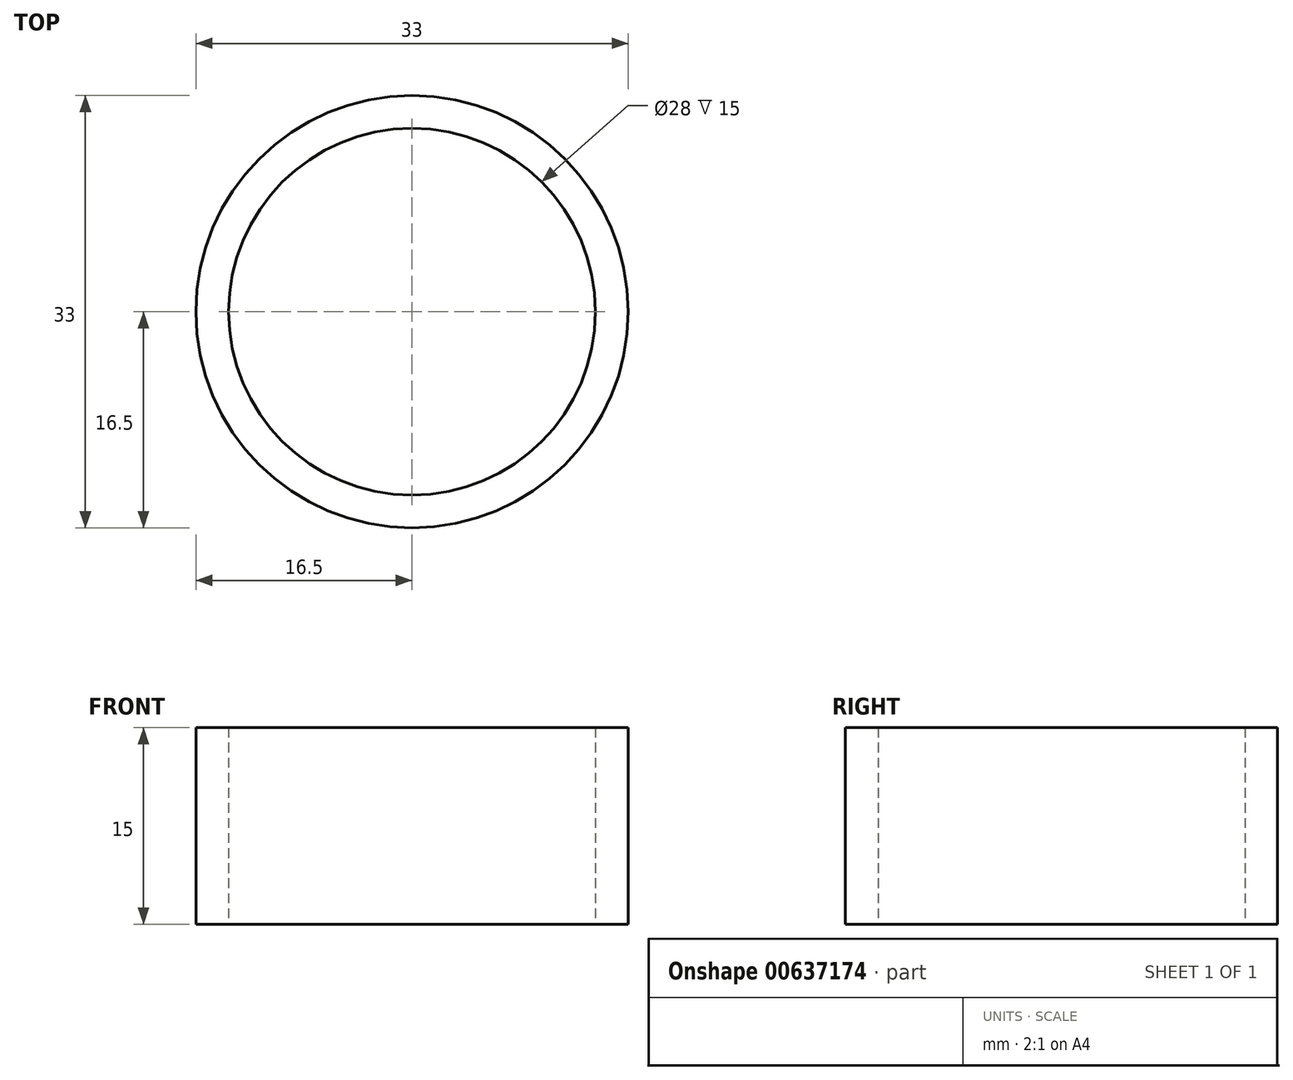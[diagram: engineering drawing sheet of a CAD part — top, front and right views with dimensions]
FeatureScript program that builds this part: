
annotation { "Feature Type Name" : "Feature", "Feature Type Description" : "" }
export const myFeature = defineFeature(function(context is Context, id is Id, definition is map)
    precondition{}
    {
        {
            var Q0;
            Q0=qCreatedBy(makeId("Top.planeOp"),FACE);
            var sketch = newSketch(context, id + "F0", { "sketchPlane" : qUnion([Q0])});
            skCircle(sketch, "E0", {"center": v(0, 0) * mm, "radius": 16.5 * mm});
            skCircle(sketch, "E1", {"center": v(0, 0) * mm, "radius": 14 * mm});
            skSolve(sketch);
        }
        {
            var Q0;
            Q0=makeQuery(id+"F0.imprint","IMPRINT",FACE,{"disambiguationData":[TD([[makeQuery(id+"F0.imprint","IMPRINT",EDGE,{"derivedFrom":sQuery(id+"F0.wireOp",EDGE,"E0")}),1.0]])]});
            extrude(context, id + "F1", {"entities" : qUnion([Q0]), "depth" : 15 * mm, "offsetDistance" : 25 * mm});
        }
    });
